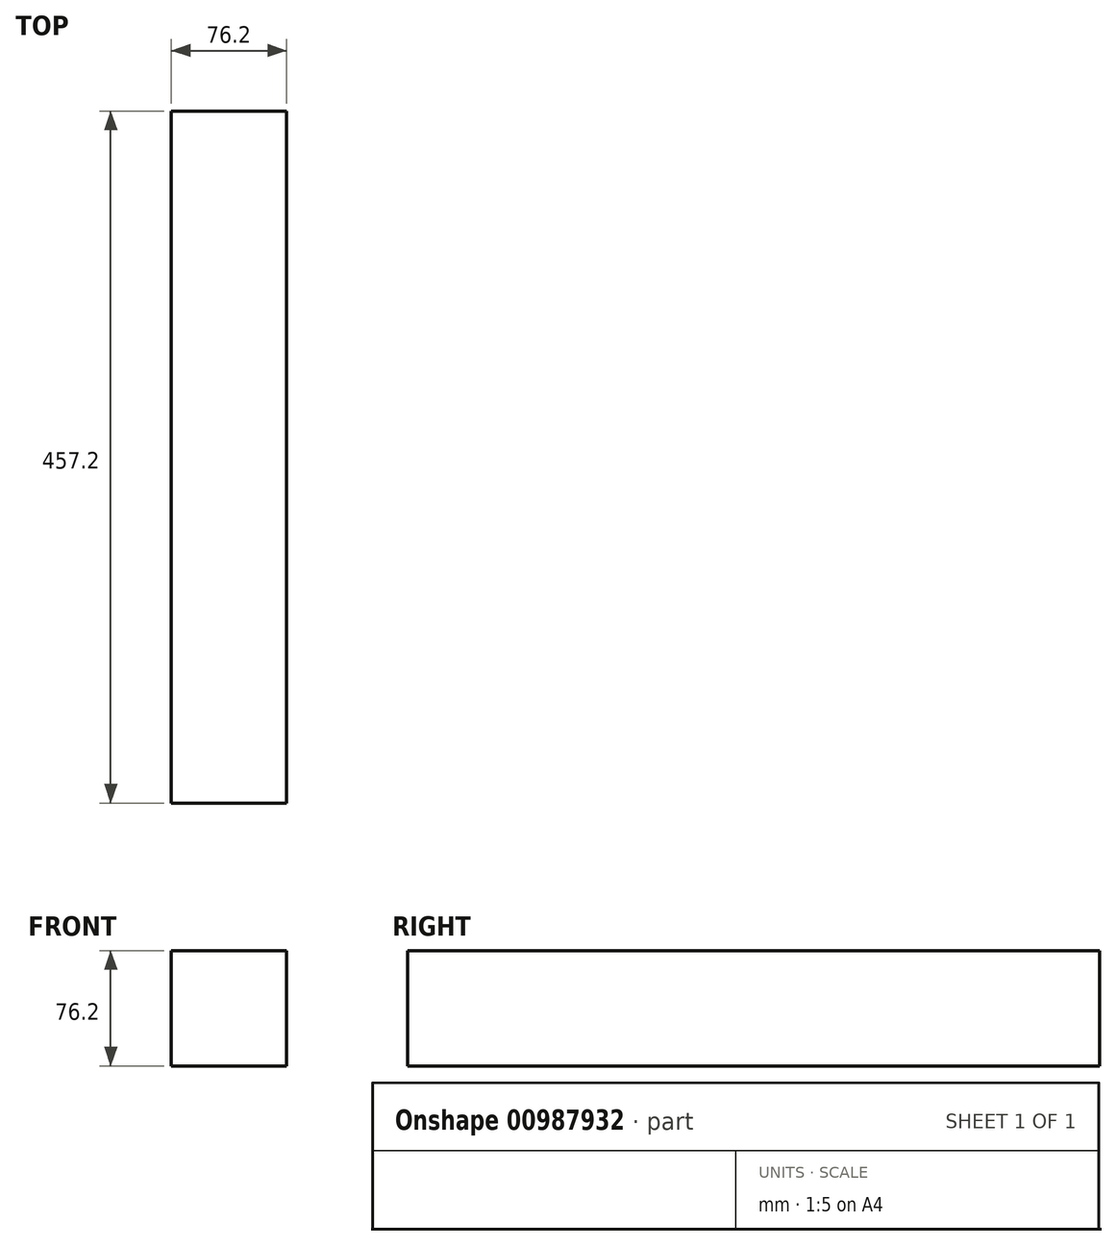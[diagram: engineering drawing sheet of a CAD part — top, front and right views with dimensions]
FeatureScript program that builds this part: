
annotation { "Feature Type Name" : "Feature", "Feature Type Description" : "" }
export const myFeature = defineFeature(function(context is Context, id is Id, definition is map)
    precondition{}
    {
        {
            var Q0;
            Q0=qCreatedBy(makeId("Front.planeOp"),FACE);
            var sketch = newSketch(context, id + "F0", { "sketchPlane" : qUnion([Q0])});
            skLineSegment(sketch, "E0.bottom", {"start": v(-84.94, 61.64) * mm, "end": v(-8.74, 61.64) * mm});
            skLineSegment(sketch, "E0.top", {"start": v(-84.94, -14.56) * mm, "end": v(-8.74, -14.56) * mm});
            skLineSegment(sketch, "E0.left", {"start": v(-84.94, 61.64) * mm, "end": v(-84.94, -14.56) * mm});
            skLineSegment(sketch, "E0.right", {"start": v(-8.74, 61.64) * mm, "end": v(-8.74, -14.56) * mm});
            skSolve(sketch);
        }
        {
            var Q0;
            Q0=makeQuery(id+"F0.imprint","IMPRINT",FACE,{"disambiguationData":[TD([[makeQuery(id+"F0.imprint","IMPRINT",EDGE,{"derivedFrom":sQuery(id+"F0.wireOp",EDGE,"E0.bottom")}),-1.0]])]});
            extrude(context, id + "F1", {"entities" : qUnion([Q0]), "depth" : 457.2 * mm, "offsetDistance" : 25.4 * mm});
        }
    });
